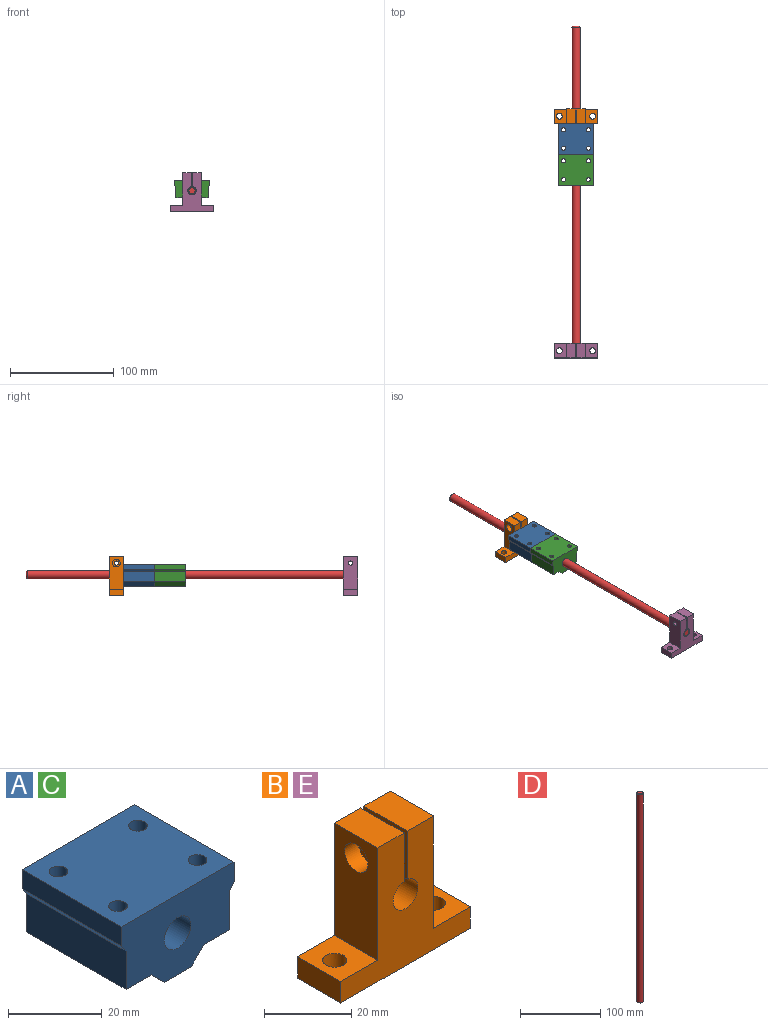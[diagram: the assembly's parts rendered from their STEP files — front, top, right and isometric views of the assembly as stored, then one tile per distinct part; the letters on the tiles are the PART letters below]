
ASSEMBLY  parts=5 mates=4
PART A: 19 faces, bbox 34x30x21 mm
  f0: plane 34x30mm, normal (0,0,1), area 969.7mm2, adj f3,f4,f13,f14,f15,f16,f17,f18
  f1: plane 30x7.6mm, normal (0,0,-1), area 202.9mm2, adj f6,f7,f13,f14,f17,f18
  f2: plane 30x7.6mm, normal (0,0,-1), area 202.9mm2, adj f9,f10,f13,f14,f15,f16
  f3: plane 30x5mm, normal (1,0,0), area 150mm2, adj f0,f11,f13,f14
  f4: plane 30x5mm, normal (-1,0,0), area 150mm2, adj f0,f5,f13,f14
  f5: plane 30x2mm, normal (-0.82,0,-0.57), area 73.2mm2, adj f4,f6,f13,f14
  f6: plane 30x10mm, normal (-1,0,0), area 300mm2, adj f1,f5,f13,f14
  f7: plane 30x4mm, normal (-0.71,0,-0.71), area 169.7mm2, adj f1,f8,f13,f14
  f8: plane 30x8mm, normal (0,0,-1), area 240mm2, adj f7,f9,f13,f14
  f9: plane 30x4mm, normal (0.71,0,-0.71), area 169.7mm2, adj f2,f8,f13,f14
  f10: plane 30x10mm, normal (1,0,0), area 300mm2, adj f2,f11,f13,f14
  f11: plane 30x2mm, normal (0.82,0,-0.57), area 73.2mm2, adj f3,f10,f13,f14
  f12: cylinder r=4mm len=30mm, axis (0,1,0), area 754mm2, adj f13,f14
  f13: plane 34x21mm, normal (0,-1,0), area 544.9mm2, adj f0,f1,f2,f3,f4,f5,f6,f7
  f14: plane 34x21mm, normal (0,1,0), area 544.9mm2, adj f0,f1,f2,f3,f4,f5,f6,f7
  f15: cylinder r=2mm len=17mm, axis (0,0,1), area 213.6mm2, adj f0,f2
  f16: cylinder r=2mm len=17mm, axis (0,0,1), area 213.6mm2, adj f0,f2
  f17: cylinder r=2mm len=17mm, axis (0,0,1), area 213.6mm2, adj f0,f1
  f18: cylinder r=2mm len=17mm, axis (0,0,1), area 213.6mm2, adj f0,f1
PART B: 20 faces, bbox 42x14x37.5 mm
  f0: cylinder r=2mm len=4mm, axis (-1,0,0), area 50.3mm2, adj f6,f19
  f1: plane 42x14mm, normal (0,0,-1), area 540.5mm2, adj f10,f11,f13,f14,f15,f16
  f2: plane 31.5x14mm, normal (1,0,0), area 428.4mm2, adj f3,f12,f13,f14,f17
  f3: plane 14x8.5mm, normal (0,0,1), area 119mm2, adj f2,f4,f13,f14
  f4: plane 14x13.53mm, normal (-1,0,0), area 176.9mm2, adj f3,f5,f13,f14,f17
  f5: cylinder r=4mm len=14mm, axis (0,1,0), area 337.8mm2, adj f4,f6,f13,f14
  f6: plane 14x13.53mm, normal (1,0,0), area 176.9mm2, adj f0,f5,f7,f13,f14
  f7: plane 14x8.5mm, normal (0,0,1), area 119mm2, adj f6,f8,f13,f14
  f8: plane 31.5x14mm, normal (-1,0,0), area 396.8mm2, adj f7,f9,f13,f14,f18
  f9: plane 14x12mm, normal (0,0,1), area 144.2mm2, adj f8,f10,f13,f14,f16
  f10: plane 14x6mm, normal (-1,0,0), area 84mm2, adj f1,f9,f13,f14
  f11: plane 14x6mm, normal (1,0,0), area 84mm2, adj f1,f12,f13,f14
  f12: plane 14x12mm, normal (0,0,1), area 144.2mm2, adj f2,f11,f13,f14,f15
  f13: plane 42x37.5mm, normal (0,-1,0), area 755.2mm2, adj f1,f2,f3,f4,f5,f6,f7,f8
  f14: plane 42x37.5mm, normal (0,1,0), area 755.2mm2, adj f1,f2,f3,f4,f5,f6,f7,f8
  f15: cylinder r=2.75mm len=6mm, axis (0,0,-1), area 103.7mm2, adj f1,f12
  f16: cylinder r=2.75mm len=6mm, axis (0,0,-1), area 103.7mm2, adj f1,f9
  f17: cylinder r=2mm len=8.5mm, axis (-1,0,0), area 106.8mm2, adj f2,f4
  f18: cylinder r=3.75mm len=7.5mm, axis (-1,0,0), area 106mm2, adj f8,f19
  f19: plane 7.5x7.5mm, normal (-1,0,0), area 31.6mm2, adj f0,f18
PART C: same geometry as A
PART D: 5 faces, bbox 8x8x320 mm
  f0: cylinder r=4mm len=318mm, axis (0,0,-1), area 7992.2mm2, adj f3,f4
  f1: plane 6x6mm, normal (0,0,1), area 28.3mm2, adj f4
  f2: plane 6x6mm, normal (0,0,-1), area 28.3mm2, adj f3
  f3: cone r=4mm half-angle=45deg, axis (0,0,1), area 31.1mm2, adj f0,f2
  f4: cone r=3mm half-angle=45deg, axis (0,0,-1), area 31.1mm2, adj f0,f1
PART E: same geometry as B
PLACE A t=(-75.72,41.49,2.97)mm
PLACE B t=(-75.72,55.49,-27.03)mm
PLACE C t=(-75.72,11.49,2.97)mm
PLACE D rot(axis=(-1,0,0),90deg) t=(-75.72,-24.51,-7.03)mm
PLACE E rot(axis=(0,0,1),180deg) t=(-75.72,-184.51,-27.03)mm
MATE fastened E.f5 <-> D.f0  axis (0,-1,0) through (-75.72,-184.51,-7.03)mm
MATE fastened C.f14 <-> A.f13  axis (0,1,0) through (-75.72,11.49,2.97)mm
MATE fastened B.f5 <-> D.f0  axis (0,1,0) through (-75.72,55.49,-7.03)mm
MATE slider D.f0 <-> A.f12  axis (0,-1,0) through (-75.72,-24.51,-7.03)mm
